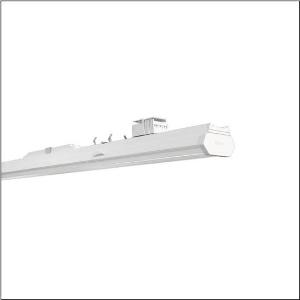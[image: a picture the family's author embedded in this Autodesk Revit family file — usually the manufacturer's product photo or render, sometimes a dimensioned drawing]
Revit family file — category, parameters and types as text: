
# Revit family: licross_11_protected_mo_51tp117n485g
name_source: partatom
category: Lighting Fixtures
units: mm (PartAtom-declared; Revit-internal decimal feet)

## family parameters
Cut with Voids When Loaded = No
Host = Face
Light Source = No
Part Type = Normal
Room Calculation Point = No
Round Connector Dimension = Use Diameter
Shared = No

## types (1)
- Licross 11 Protected MO (1 x LED, 8680 lm, 48.6 W, 4000K)
    Apparent Load = 49 VA
    CIE Flux Codes = 83 94 98 100 100
    Color Rendering = 80
    Color Temperature = 4000K
    Default Elevation = 1800 mm
    Description = Licross 11 Protected MO, luminaire insert, of sheet steel, galvanised, coil coated, white, length: 1.500mm, width: 90mm, height: 101mm, LED rated luminous flux: 8.680lm, light colour: 840, SDCM (Standard Deviation of Colour Matching)MacAdam ≤ 2 SDCM (initial), control gear: ON/OFF, with plug, 3-pole, with phase selection, mains connection: 220..240V, AC, 50/60Hz, rated input power: 49W, internal wiring halogen-free, primary light control with lens, of plastic, primary optical cover: cover, of PMMA, light emission: direct distribution, primary light characteristic: symmetric, protection rating (complete): IP64, insulation class (complete): insulation class I (protective earthing), certification: CE, ENEC, VDE, UKCA, protection symbol: D if used in an environment with conductive dust loads with corresponding accessories, impact resistance: IK06, permissible ambient temperature for indoor applications: -25..+35°C, corresponds to IFS (International Featured Standards) requirements for safety and quality in the food industry, reducing of maximum allowable ambient temperature of 5°C with ceiling mounting, LABS conformity tested according to VDMA 24364:2018-05, The light source and the operating device comply with the requirements of the Ecodesign Regulation (EU) 2019/2020 and are replaceable in accordance with this regulation, packaging unit: 1 piece
    Height = 92 mm
    Lamp = 1 x LED
    Lamp Light Flux = 8680 lm
    Lamp Power = 48.6 W
    Lamp count = 1
    Length = 1500 mm
    Luminous efficacy = 179 lm/W
    Manufacturer = Siteco
    ModVariant = No
    Model = 51TP117N485G
    Mounting Place = Ceiling
    Mounting Type = Pendant
    Number of Poles = 1
    OnlyDefault = Yes
    Power Factor = 1
    Product Name = Licross 11 Protected MO
    Product group = luminaire insert | ceiling pendant
    ProductGroupID = 901
    Protection Class = Protection class I
    Protection Degree = IP 64
    RLX_Detail_Level = 1
    RLX_Emergency_Light_Flux = 0 lm
    RLX_Emergency_Type = 0
    RLX_Emergency_Type_DB = No
    RlxData = <blob elided: 20749 chars, md5=81483eee>
    Socket = socket
    Standby Power = 0 W
    System Light Flux = 8680 lm
    System Power = 49 W
    Type Comments = Product without accessories
    Type Image = l_1256148.jpg
    URL = http://relux.com
    VarID = ---
    Voltage = 0 V
    Weight = 0.00 kg
    Width = 88 mm

## geometry (parser evidence)
native form markers: Blend x4, Sweep x11
no freeform markers — native parametric forms only
